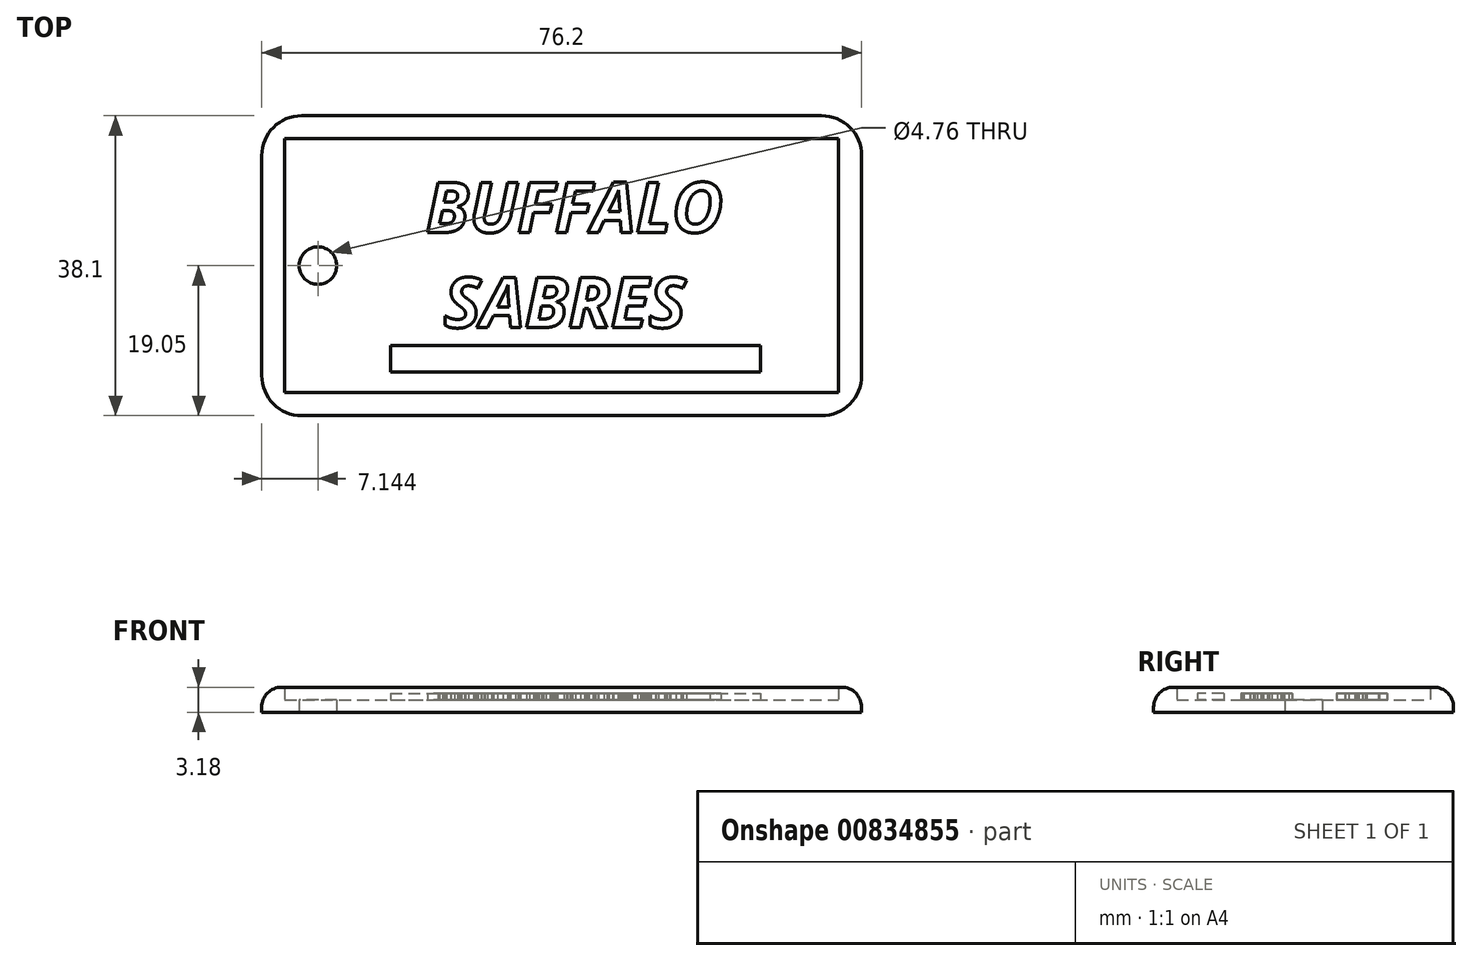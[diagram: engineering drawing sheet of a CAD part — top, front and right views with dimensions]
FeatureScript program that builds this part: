
annotation { "Feature Type Name" : "Feature", "Feature Type Description" : "" }
export const myFeature = defineFeature(function(context is Context, id is Id, definition is map)
    precondition{}
    {
        {
            var Q0;
            Q0=qCreatedBy(makeId("Top.planeOp"),FACE);
            var sketch = newSketch(context, id + "F0", { "sketchPlane" : qUnion([Q0])});
            skLineSegment(sketch, "E0.bottom", {"start": v(0, 0) * mm, "end": v(76.2, 0) * mm});
            skLineSegment(sketch, "E0.top", {"start": v(0, 38.1) * mm, "end": v(76.2, 38.1) * mm});
            skLineSegment(sketch, "E0.left", {"start": v(0, 0) * mm, "end": v(0, 38.1) * mm});
            skLineSegment(sketch, "E0.right", {"start": v(76.2, 0) * mm, "end": v(76.2, 38.1) * mm});
            skCircle(sketch, "E1", {"center": v(7.14, 19.05) * mm, "radius": 2.38 * mm});
            skPoint(sketch, "E1.centerSnap0", {"position": v(0, 19.05) * mm});
            skLineSegment(sketch, "E2.0", {"start": v(2.92, 35.18) * mm, "end": v(73.28, 35.18) * mm});
            skLineSegment(sketch, "E2.1", {"start": v(2.92, 2.92) * mm, "end": v(2.92, 35.18) * mm});
            skLineSegment(sketch, "E2.2", {"start": v(2.92, 2.92) * mm, "end": v(73.28, 2.92) * mm});
            skLineSegment(sketch, "E2.3", {"start": v(73.28, 2.92) * mm, "end": v(73.28, 35.18) * mm});
            skSolve(sketch);
        }
        {
            var Q0;
            Q0=makeQuery(id+"F0.imprint","IMPRINT",FACE,{"disambiguationData":[TD([[makeQuery(id+"F0.imprint","IMPRINT",EDGE,{"derivedFrom":sQuery(id+"F0.wireOp",EDGE,"E1")}),-1.0]])]});
            extrude(context, id + "F1", {"entities" : qUnion([Q0]), "depth" : 1.59 * mm, "offsetDistance" : 25.4 * mm});
        }
        {
            var Q0;
            Q0=qSketchRegion(id+"F0",true);
            extrude(context, id + "F2", {"entities" : qUnion([Q0]), "operationType" : NewBodyOperationType.ADD, "depth" : 3.17 * mm, "offsetDistance" : 25.4 * mm});
        }
        {
            var Q0;
            Q0=makeQuery(id+"F2.opExtrude","SWEPT_EDGE",EDGE,{"disambiguationData":[OSD([sQuery(id+"F0.wireOp",EDGE,"E0.bottom"),sQuery(id+"F0.wireOp",EDGE,"E0.right")])]});
            var Q1;
            Q1=makeQuery(id+"F2.opExtrude","SWEPT_EDGE",EDGE,{"disambiguationData":[OSD([sQuery(id+"F0.wireOp",EDGE,"E0.bottom"),sQuery(id+"F0.wireOp",EDGE,"E0.left")])]});
            var Q2;
            Q2=makeQuery(id+"F2.opExtrude","SWEPT_EDGE",EDGE,{"disambiguationData":[OSD([sQuery(id+"F0.wireOp",EDGE,"E0.top"),sQuery(id+"F0.wireOp",EDGE,"E0.right")])]});
            var Q3;
            Q3=makeQuery(id+"F2.opExtrude","SWEPT_EDGE",EDGE,{"disambiguationData":[OSD([sQuery(id+"F0.wireOp",EDGE,"E0.top"),sQuery(id+"F0.wireOp",EDGE,"E0.left")])]});
            fillet(context, id + "F3", {"entities" : qUnion([Q0, Q1, Q2, Q3]), "radius" : 5.08 * mm, "tangentPropagation" : true, "allowEdgeOverflow" : false});
        }
        {
            var Q0;
            Q0=makeQuery(id+"F2.opExtrude","CAP_EDGE",EDGE,{"disambiguationData":[OSD([sQuery(id+"F0.wireOp",EDGE,"E0.bottom")])],"isStart":false});
            fillet(context, id + "F4", {"entities" : qUnion([Q0]), "radius" : 2.54 * mm, "tangentPropagation" : true, "allowEdgeOverflow" : false});
        }
        {
            var Q0;
            Q0=makeQuery(id+"F1.opExtrude","CAP_FACE",FACE,{"disambiguationData":[OSD([sQuery(id+"F0.wireOp",EDGE,"E1"),sQuery(id+"F0.wireOp",EDGE,"E2.0"),sQuery(id+"F0.wireOp",EDGE,"E2.1"),sQuery(id+"F0.wireOp",EDGE,"E2.2"),sQuery(id+"F0.wireOp",EDGE,"E2.3")])],"isStart":false});
            var sketch = newSketch(context, id + "F5", { "sketchPlane" : qUnion([Q0])});
            skLineSegment(sketch, "E3.bottom", {"start": v(16.34, 8.92) * mm, "end": v(63.35, 8.92) * mm});
            skLineSegment(sketch, "E3.top", {"start": v(16.34, 5.54) * mm, "end": v(63.35, 5.54) * mm});
            skLineSegment(sketch, "E3.left", {"start": v(16.34, 8.92) * mm, "end": v(16.34, 5.54) * mm});
            skLineSegment(sketch, "E3.right", {"start": v(63.35, 8.92) * mm, "end": v(63.35, 5.54) * mm});
            skText(sketch, "E4", { "text": "BUFFALO\n SABRES", "fontName": "OpenSans-BoldItalic.ttf"});
            const initialGuessF5  = {"E4": [0.02082, 0.02327, 1, 0, 0.0064]};
            skSetInitialGuess(sketch, initialGuessF5);
            skSolve(sketch);
        }
        {
            var Q0;
            Q0 = qSketchRegion(id + "F5", true);
            extrude(context, id + "F6", {"entities" : qUnion([Q0]), "operationType" : NewBodyOperationType.ADD, "depth" : 0.8 * mm, "offsetDistance" : 25.4 * mm});
        }
    });
